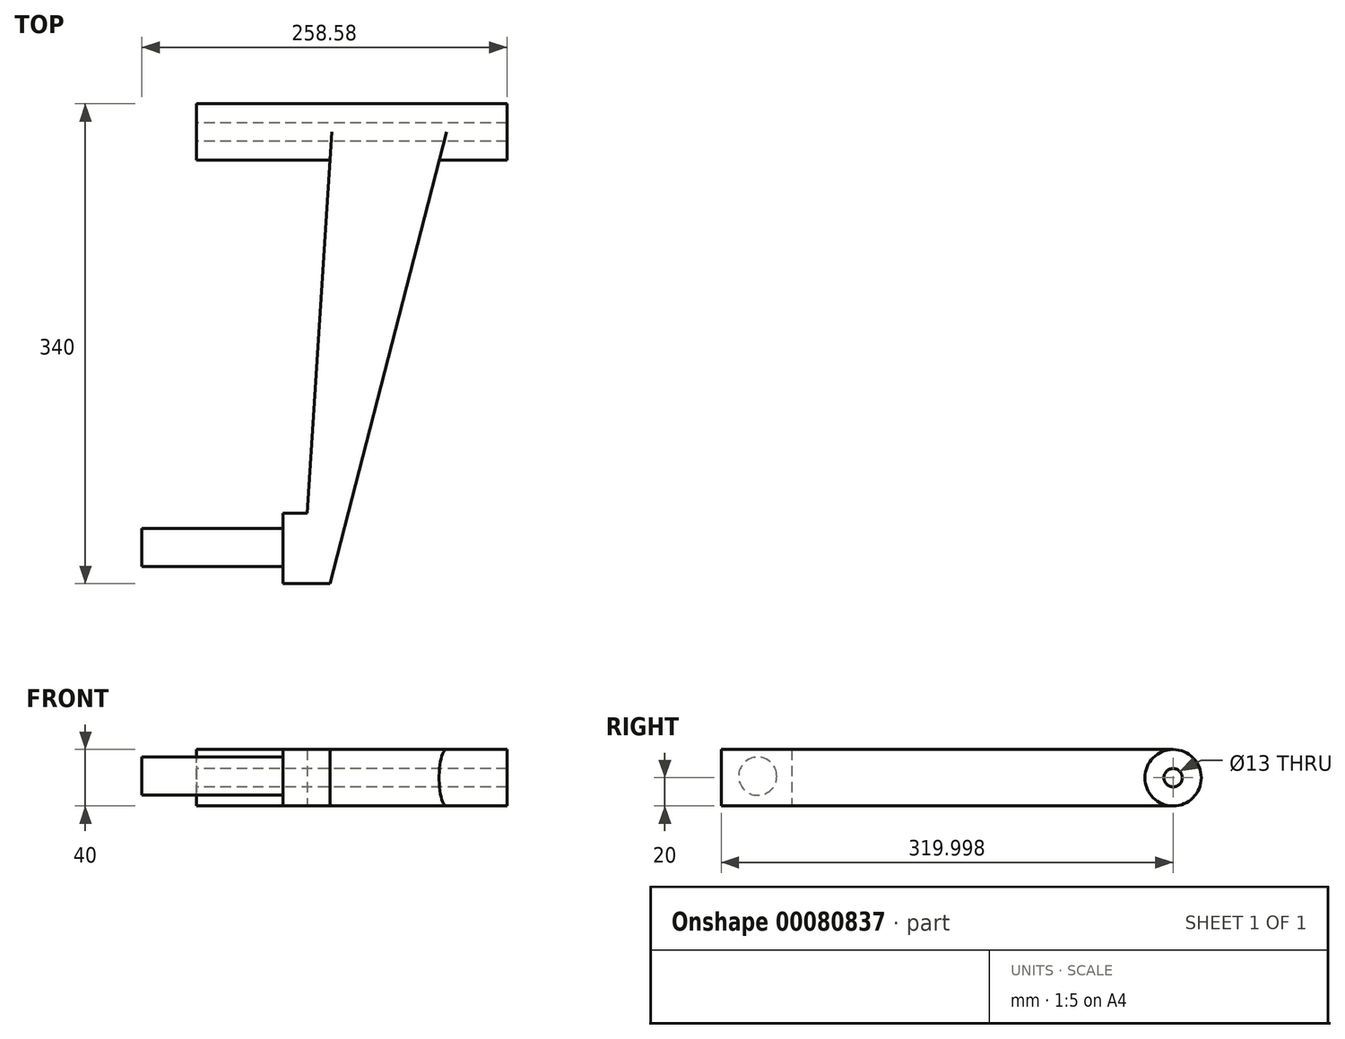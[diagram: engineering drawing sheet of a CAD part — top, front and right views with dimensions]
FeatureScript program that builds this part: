
annotation { "Feature Type Name" : "Feature", "Feature Type Description" : "" }
export const myFeature = defineFeature(function(context is Context, id is Id, definition is map)
    precondition{}
    {
        {
            var Q0;
            Q0=qCreatedBy(makeId("Top.planeOp"),FACE);
            var sketch = newSketch(context, id + "F0", { "sketchPlane" : qUnion([Q0])});
            skLineSegment(sketch, "E0", {"start": v(-94.52, 235.24) * mm, "end": v(125.48, 235.24) * mm});
            skLineSegment(sketch, "E1", {"start": v(125.48, 235.24) * mm, "end": v(125.48, 195.24) * mm});
            skLineSegment(sketch, "E2", {"start": v(125.48, 195.24) * mm, "end": v(77.38, 195.24) * mm});
            skLineSegment(sketch, "E3", {"start": v(77.38, 195.24) * mm, "end": v(0, -104.76) * mm});
            skLineSegment(sketch, "E4", {"start": v(0, -104.76) * mm, "end": v(-33.1, -104.76) * mm});
            skLineSegment(sketch, "E5", {"start": v(-33.1, -104.76) * mm, "end": v(-33.1, -54.76) * mm});
            skLineSegment(sketch, "E6", {"start": v(-33.1, -54.76) * mm, "end": v(-15.95, -54.76) * mm});
            skLineSegment(sketch, "E7", {"start": v(-15.95, -54.76) * mm, "end": v(0, 195.24) * mm});
            skLineSegment(sketch, "E8", {"start": v(0, 195.24) * mm, "end": v(-94.52, 195.24) * mm});
            skLineSegment(sketch, "E9", {"start": v(-94.52, 195.24) * mm, "end": v(-94.52, 235.24) * mm});
            skSolve(sketch);
        }
        {
            var Q0;
            Q0=makeQuery(id+"F0.imprint","IMPRINT",FACE,{"disambiguationData":[TD([[makeQuery(id+"F0.imprint","IMPRINT",EDGE,{"derivedFrom":sQuery(id+"F0.wireOp",EDGE,"E0")}),-1.0]])]});
            extrude(context, id + "F1", {"entities" : qUnion([Q0]), "depth" : 40 * mm});
        }
        {
            var Q0;
            Q0=makeQuery(id+"F1.opExtrude","CAP_EDGE",EDGE,{"disambiguationData":[OSD([sQuery(id+"F0.wireOp",EDGE,"E0")])],"isStart":false});
            var Q1;
            Q1=makeQuery(id+"F1.opExtrude","CAP_EDGE",EDGE,{"disambiguationData":[OSD([sQuery(id+"F0.wireOp",EDGE,"E0")])],"isStart":true});
            var Q2;
            Q2=makeQuery(id+"F1.opExtrude","CAP_EDGE",EDGE,{"disambiguationData":[OSD([sQuery(id+"F0.wireOp",EDGE,"E8")])],"isStart":true});
            var Q3;
            Q3=makeQuery(id+"F1.opExtrude","CAP_EDGE",EDGE,{"disambiguationData":[OSD([sQuery(id+"F0.wireOp",EDGE,"E8")])],"isStart":false});
            var Q4;
            Q4=makeQuery(id+"F1.opExtrude","CAP_EDGE",EDGE,{"disambiguationData":[OSD([sQuery(id+"F0.wireOp",EDGE,"E2")])],"isStart":true});
            var Q5;
            Q5=makeQuery(id+"F1.opExtrude","CAP_EDGE",EDGE,{"disambiguationData":[OSD([sQuery(id+"F0.wireOp",EDGE,"E2")])],"isStart":false});
            fillet(context, id + "F2", {"entities" : qUnion([Q0, Q1, Q2, Q3, Q4, Q5]), "radius" : 20 * mm, "tangentPropagation" : true, "allowEdgeOverflow" : false});
        }
        {
            var Q0;
            Q0=makeQuery(id+"F1.opExtrude","SWEPT_FACE",FACE,{"disambiguationData":[OSD([sQuery(id+"F0.wireOp",EDGE,"E9")])]});
            var sketch = newSketch(context, id + "F3", { "sketchPlane" : qUnion([Q0])});
            skCircle(sketch, "E10", {"center": v(-215.24, 20) * mm, "radius": 6.5 * mm});
            skSolve(sketch);
        }
        {
            var Q0;
            Q0=makeQuery(id+"F3.imprint","IMPRINT",FACE,{"disambiguationData":[TD([[makeQuery(id+"F3.imprint","IMPRINT",EDGE,{"derivedFrom":sQuery(id+"F3.wireOp",EDGE,"E10")}),1.0]])]});
            extrude(context, id + "F4", {"entities" : qUnion([Q0]), "operationType" : NewBodyOperationType.REMOVE, "endBound" : BoundingType.THROUGH_ALL, "oppositeDirection" : true, "depth" : 25 * mm});
        }
        {
            var Q0;
            Q0=makeQuery(id+"F1.opExtrude","SWEPT_FACE",FACE,{"disambiguationData":[OSD([sQuery(id+"F0.wireOp",EDGE,"E5")])]});
            var sketch = newSketch(context, id + "F5", { "sketchPlane" : qUnion([Q0])});
            skCircle(sketch, "E11", {"center": v(79, 21.1) * mm, "radius": 13.52 * mm});
            skSolve(sketch);
        }
        {
            var Q0;
            Q0=makeQuery(id+"F5.imprint","IMPRINT",FACE,{"disambiguationData":[TD([[makeQuery(id+"F5.imprint","IMPRINT",EDGE,{"derivedFrom":sQuery(id+"F5.wireOp",EDGE,"E11")}),1.0]])]});
            extrude(context, id + "F6", {"entities" : qUnion([Q0]), "operationType" : NewBodyOperationType.ADD, "depth" : 100 * mm});
        }
    });
